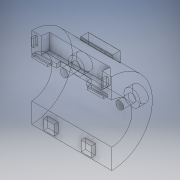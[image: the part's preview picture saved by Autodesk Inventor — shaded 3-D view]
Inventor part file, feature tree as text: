
AUTODESK INVENTOR PART (.ipt)
format: ipt  version: 2018 (Build 220112000, 112)  size: 264,192 bytes
history: native  units: in
note: dims shown in document units (in); Inventor stores cm internally (conversion verified against a paired STEP export)
features: extrude x9, sketch x9, plane x3, fillet x1
ambient origin geometry x8: Origin, YZ Plane, XZ Plane, XY Plane, X Axis, Y Axis, Z Axis, Center Point
bodies: Solid1 (feature_tree)
feature tree (22):
  extrude  "Extrusion1"  Depth=1.0in
  plane  "Work Plane2"
  extrude  "Extrusion7"  Depth=0.5in
  extrude  "Extrusion9"  TaperAngle=90.0deg  [1 undecoded]
  extrude  "Extrusion10"  Depth=0.3in
  plane  "Work Plane6"
  extrude  "Extrusion13"  Depth=0.4in
  extrude  "Extrusion15"  Depth=0.2in TaperAngle=0.0deg
  extrude  "Extrusion16"  Depth=0.19in
  plane  "Work Plane5"
  extrude  "Extrusion17"  Depth=0.3in
  extrude  "Extrusion18"  TaperAngle=0.0deg  [1 undecoded]
  fillet  "Fillet5"  [1 undecoded]
  sketch  "Sketch1"  dims[d0=1.0in d1=0.5in]
  sketch  "Sketch10"  dims[d5=0.5in d6=0.5in]
  sketch  "Sketch12"  dims[d7=270.0deg d8=90.0deg]
  sketch  "Sketch13"  dims[d9=1.9685in d10=0.0in d62=0.3in]
  sketch  "Sketch16"  dims[d63=0.3in d66=0.4in]
  sketch  "Sketch18"  dims[d67=0.4in d68=0.2in d69=0.0in]
  sketch  "Sketch19"  dims[d78=0.19in d79=0.19in]
  sketch  "Sketch20"  dims[d82=0.3in d83=0.3in]
  sketch  "Sketch21"  dims[d84=2.0in d85=0.0in d86=0.0in d87=0.0in d88=0.0in d89=0.0in d90=0.4in d92=0.4in d93=0.1in d95=0.1in d96=0.0in d105=0.025in d106=0.025in d107=0.1in d108=0.05in d109=0.75in d110=0.2in d111=1.0in d112=0.0in d133=0.05in d134=0.2in d135=0.05in d136=0.2in d137=0.09in d138=0.05in d139=0.09in d140=0.05in d141=0.1in d142=0.0in d143=0.25in d144=0.25in d145=0.125in d146=0.4in d147=0.4in d148=0.25in d149=0.25in d150=0.125in d151=0.1in d152=0.0in d153=1.5in d154=0.4in d155=0.4in d156=0.0in d166=0.7874in d167=0.0in d172=45.0deg d173=0.2in d174=0.1in d175=0.3in d176=0.15in d177=0.01in]
note: 3 required parameter values undecoded (feature->parameter linkage not recoverable at this tier; creation-order binding heuristic only, values carry confidence <= 0.55)
